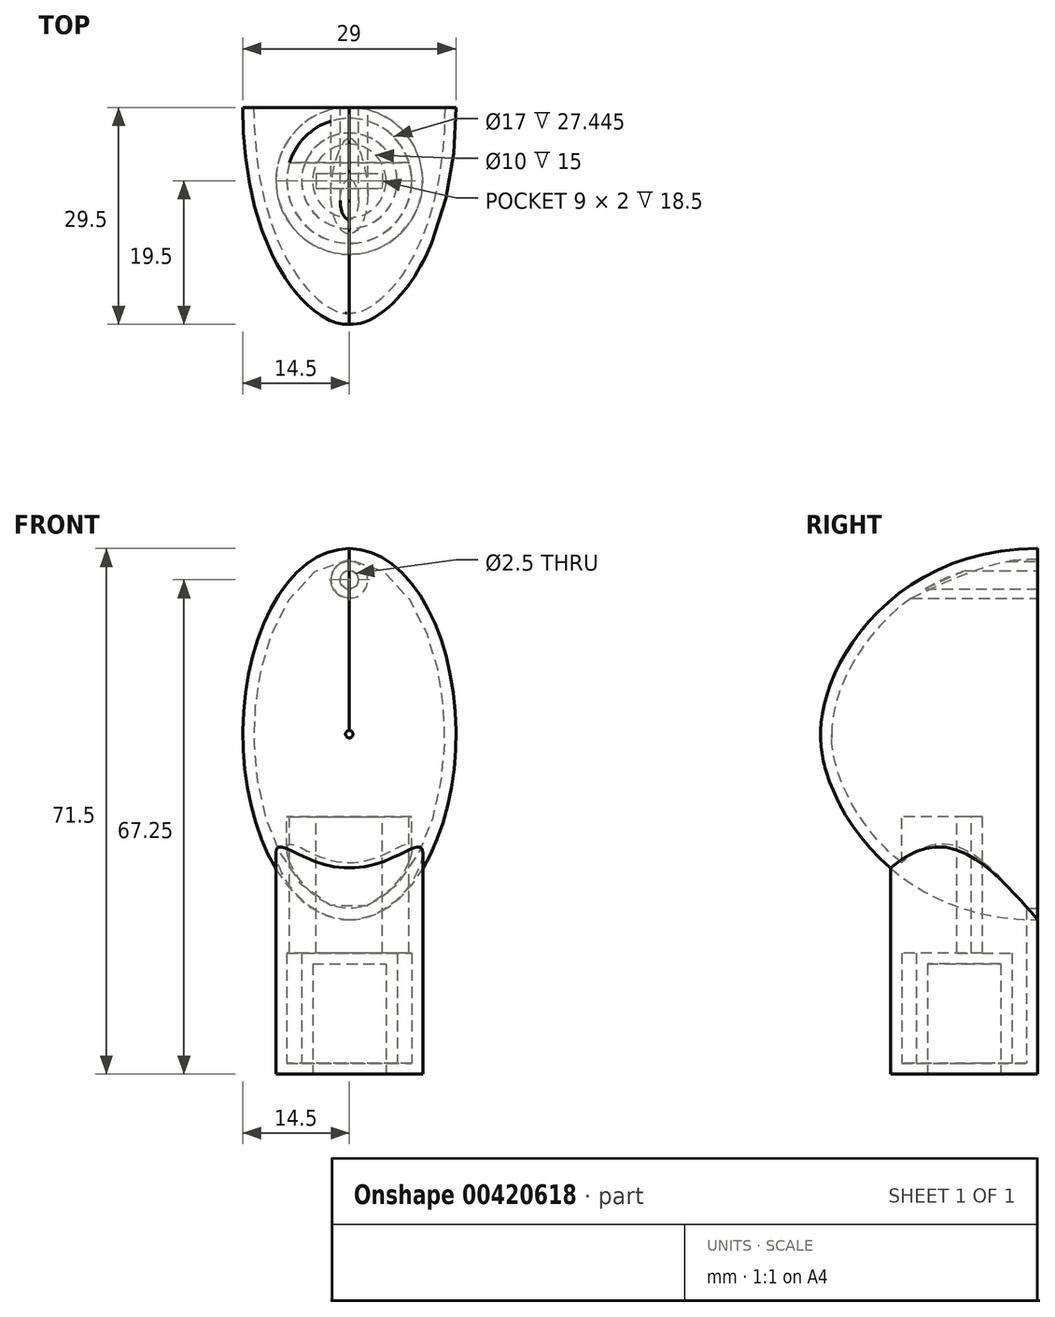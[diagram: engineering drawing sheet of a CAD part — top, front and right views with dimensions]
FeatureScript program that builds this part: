
annotation { "Feature Type Name" : "Feature", "Feature Type Description" : "" }
export const myFeature = defineFeature(function(context is Context, id is Id, definition is map)
    precondition{}
    {
        {
            var Q0;
            Q0=qCreatedBy(makeId("Front.planeOp"),FACE);
            var sketch = newSketch(context, id + "F0", { "sketchPlane" : qUnion([Q0])});
            skLineSegment(sketch, "E0", {"start": v(0, 0) * mm, "end": v(0, 64.1) * mm, "construction": true});
            skLineSegment(sketch, "E1", {"start": v(-10, 0) * mm, "end": v(-10, 45) * mm});
            skLineSegment(sketch, "E2", {"start": v(-10, 45) * mm, "end": v(0, 45) * mm});
            skLineSegment(sketch, "E3", {"start": v(-10, 0) * mm, "end": v(-5, 0) * mm});
            skLineSegment(sketch, "E4", {"start": v(-5, 0) * mm, "end": v(-5, 15) * mm});
            skLineSegment(sketch, "E5", {"start": v(-5, 15) * mm, "end": v(0, 15) * mm});
            skLineSegment(sketch, "E6", {"start": v(0, 15) * mm, "end": v(0, 45) * mm});
            skLineSegment(sketch, "E7", {"start": v(-5, 0) * mm, "end": v(0, 0) * mm, "construction": true});
            skSolve(sketch);
        }
        {
            var Q0;
            Q0 = qSketchRegion(id + "F0", true);
            var Q1;
            Q1=sQuery(id+"F0.wireOp",EDGE,"E0");
            revolve(context, id + "F1", {"entities" : qUnion([Q0]), "axis" : qUnion([Q1]), "revolveType" : RevolveType.FULL});
        }
        {
            var Q0;
            Q0=qCreatedBy(makeId("Right.planeOp"),FACE);
            var sketch = newSketch(context, id + "F2", { "sketchPlane" : qUnion([Q0])});
            skLineSegment(sketch, "E8", {"start": v(-20, 46.25) * mm, "end": v(10, 46.25) * mm});
            skLineSegment(sketch, "E9", {"start": v(-20, 46.25) * mm, "end": v(-20, 81.64) * mm, "construction": true});
            skLineSegment(sketch, "E10", {"start": v(10, 46.25) * mm, "end": v(10, 71.5) * mm});
            skLineSegment(sketch, "E11", {"start": v(34.13, 74.9) * mm, "end": v(10, 71.5) * mm, "construction": true});
            skLineSegment(sketch, "E12", {"start": v(10, 71.5) * mm, "end": v(-44.83, 71.5) * mm, "construction": true});
            skArc(sketch, "E13", {"start": v(10, 71.5) * mm, "mid": v(-8.63, 63.19) * mm, "end": v(-20, 46.25) * mm, "construction": true});
            skLineSegment(sketch, "E14", {"start": v(10, 46.25) * mm, "end": v(64.99, 46.25) * mm, "construction": true});
            skArc(sketch, "E15", {"start": v(-18.93, 50.74) * mm, "mid": v(-19.73, 48.56) * mm, "end": v(-20, 46.25) * mm});
            skArc(sketch, "E16", {"start": v(10, 71.5) * mm, "mid": v(-7.02, 64.68) * mm, "end": v(-18.93, 50.74) * mm});
            skSolve(sketch);
        }
        {
            var Q0;
            Q0=qCreatedBy(makeId("Front.planeOp"),FACE);
            cPlane(context, id + "F3", {"entities" : qUnion([Q0]), "cplaneType" : CPlaneType.OFFSET, "offset" : 10 * mm, "oppositeDirection" : true, "width" : 150 * mm, "height" : 150 * mm});
        }
        {
            var Q0;
            Q0=qCreatedBy(id+"F3.planeOp",FACE);
            cPlane(context, id + "F4", {"entities" : qUnion([Q0]), "cplaneType" : CPlaneType.OFFSET, "offset" : 29.5 * mm, "width" : 150 * mm, "height" : 150 * mm});
        }
        {
            var Q0;
            Q0=qCreatedBy(id+"F3.planeOp",FACE);
            var sketch = newSketch(context, id + "F5", { "sketchPlane" : qUnion([Q0])});
            skEllipse(sketch, "E17", {"center": v(0, 46.25) * mm, "majorRadius": 25.25 * mm, "minorRadius": 14.5 * mm, "majorAxis": v(0, 1)});
            skSolve(sketch);
        }
        {
            var Q0;
            Q0=qCreatedBy(id+"F4.planeOp",FACE);
            var sketch = newSketch(context, id + "F6", { "sketchPlane" : qUnion([Q0])});
            skCircle(sketch, "E18", {"center": v(0, 46.25) * mm, "radius": 0.5 * mm});
            skSolve(sketch);
        }
        {
            var Q1;
            Q1=makeQuery(id+"F5.imprint","IMPRINT",FACE,{"disambiguationData":[TD([[makeQuery(id+"F5.imprint","IMPRINT",EDGE,{"derivedFrom":sQuery(id+"F5.wireOp",EDGE,"E17")}),1.0]])]});
            var Q2;
            Q2=makeQuery(id+"F6.imprint","IMPRINT",FACE,{"disambiguationData":[TD([[makeQuery(id+"F6.imprint","IMPRINT",EDGE,{"derivedFrom":sQuery(id+"F6.wireOp",EDGE,"E18")}),1.0]])]});
            loft(context, id + "F7", {"operationType" : NewBodyOperationType.ADD, "startCondition" : LoftEndDerivativeType.NORMAL_TO_PROFILE, "startMagnitude" : 2, "endCondition" : LoftEndDerivativeType.TANGENT_TO_PROFILE, "endMagnitude" : 1, "sheetProfilesArray" : [{ "sheetProfileEntities" : qUnion([Q1]) }, { "sheetProfileEntities" : qUnion([Q2]) }]});
        }
        {
            var Q0;
            Q0=makeQuery(id+"F7.opLoft","CAP_FACE",FACE,{"disambiguationData":[OSD([makeQuery(id+"F5.imprint","IMPRINT",FACE,{"disambiguationData":[TD([[makeQuery(id+"F5.imprint","IMPRINT",EDGE,{"derivedFrom":sQuery(id+"F5.wireOp",EDGE,"E17")}),1.0]])]})])],"isStart":true});
            shell(context, id + "F8", {"entities" : qUnion([Q0]), "thickness" : 1.5 * mm});
        }
        {
            var Q0;
            Q0=makeQuery(id+"F7.opLoft","CAP_FACE",FACE,{"disambiguationData":[OSD([makeQuery(id+"F5.imprint","IMPRINT",FACE,{"disambiguationData":[TD([[makeQuery(id+"F5.imprint","IMPRINT",EDGE,{"derivedFrom":sQuery(id+"F5.wireOp",EDGE,"E17")}),1.0]])]})])],"isStart":true});
            var sketch = newSketch(context, id + "F9", { "sketchPlane" : qUnion([Q0])});
            skCircle(sketch, "E19", {"center": v(0, 67.25) * mm, "radius": 2.5 * mm});
            skCircle(sketch, "E20", {"center": v(0, 67.25) * mm, "radius": 1.25 * mm});
            skSolve(sketch);
        }
        {
            var Q0;
            Q0=makeQuery(id+"F9.imprint","IMPRINT",FACE,{"disambiguationData":[TD([[makeQuery(id+"F9.imprint","IMPRINT",EDGE,{"derivedFrom":sQuery(id+"F9.wireOp",EDGE,"E19")}),1.0]])]});
            extrude(context, id + "F10", {"entities" : qUnion([Q0]), "operationType" : NewBodyOperationType.ADD, "endBound" : BoundingType.UP_TO_NEXT, "oppositeDirection" : true, "depth" : 25 * mm, "offsetDistance" : 25 * mm});
        }
        {
            var Q0;
            Q0=makeQuery(id+"F1.opRevolve","SWEPT_FACE",FACE,{"disambiguationData":[OSD([sQuery(id+"F0.wireOp",EDGE,"E3")])]});
            cPlane(context, id + "F11", {"entities" : qUnion([Q0]), "cplaneType" : CPlaneType.OFFSET, "offset" : 35 * mm, "oppositeDirection" : true, "width" : 150 * mm, "height" : 150 * mm});
        }
        {
            var Q0;
            Q0=qCreatedBy(id+"F11.planeOp",FACE);
            var sketch = newSketch(context, id + "F12", { "sketchPlane" : qUnion([Q0])});
            skLineSegment(sketch, "E21.bottom", {"start": v(-4.5, -1) * mm, "end": v(4.5, -1) * mm});
            skLineSegment(sketch, "E21.top", {"start": v(-4.5, 1) * mm, "end": v(4.5, 1) * mm});
            skLineSegment(sketch, "E21.left", {"start": v(-4.5, -1) * mm, "end": v(-4.5, 1) * mm});
            skLineSegment(sketch, "E21.right", {"start": v(4.5, -1) * mm, "end": v(4.5, 1) * mm});
            skPoint(sketch, "E21.middle", {"position": v(0, 0) * mm});
            skArc(sketch, "E22", {"start": v(8.12, -2.5) * mm, "mid": v(0, 8.5) * mm, "end": v(-8.12, -2.5) * mm});
            skLineSegment(sketch, "E23", {"start": v(-8.12, -2.5) * mm, "end": v(8.12, -2.5) * mm});
            skSolve(sketch);
        }
        {
            var Q0;
            Q0 = qSketchRegion(id + "F12", true);
            var Q1;
            Q1=makeQuery(id+"F8.opShell","OFFSET_FACE",FACE,{"disambiguationData":[OSD([sQuery(id+"F0.wireOp",EDGE,"E5")])]});
            extrude(context, id + "F13", {"entities" : qUnion([Q0]), "operationType" : NewBodyOperationType.ADD, "endBound" : BoundingType.UP_TO_SURFACE, "depth" : 25 * mm, "endBoundEntityFace" : qUnion([Q1]), "offsetDistance" : 25 * mm});
        }
        {
            var Q0;
            Q0=makeQuery(id+"F7.opLoft","CAP_FACE",FACE,{"disambiguationData":[OSD([makeQuery(id+"F5.imprint","IMPRINT",FACE,{"disambiguationData":[TD([[makeQuery(id+"F5.imprint","IMPRINT",EDGE,{"derivedFrom":sQuery(id+"F5.wireOp",EDGE,"E17")}),1.0]])]})])],"isStart":true});
            cPlane(context, id + "F15", {"entities" : qUnion([Q0]), "cplaneType" : CPlaneType.OFFSET, "offset" : 14 * mm, "oppositeDirection" : true, "width" : 150 * mm, "height" : 150 * mm});
        }
    });
